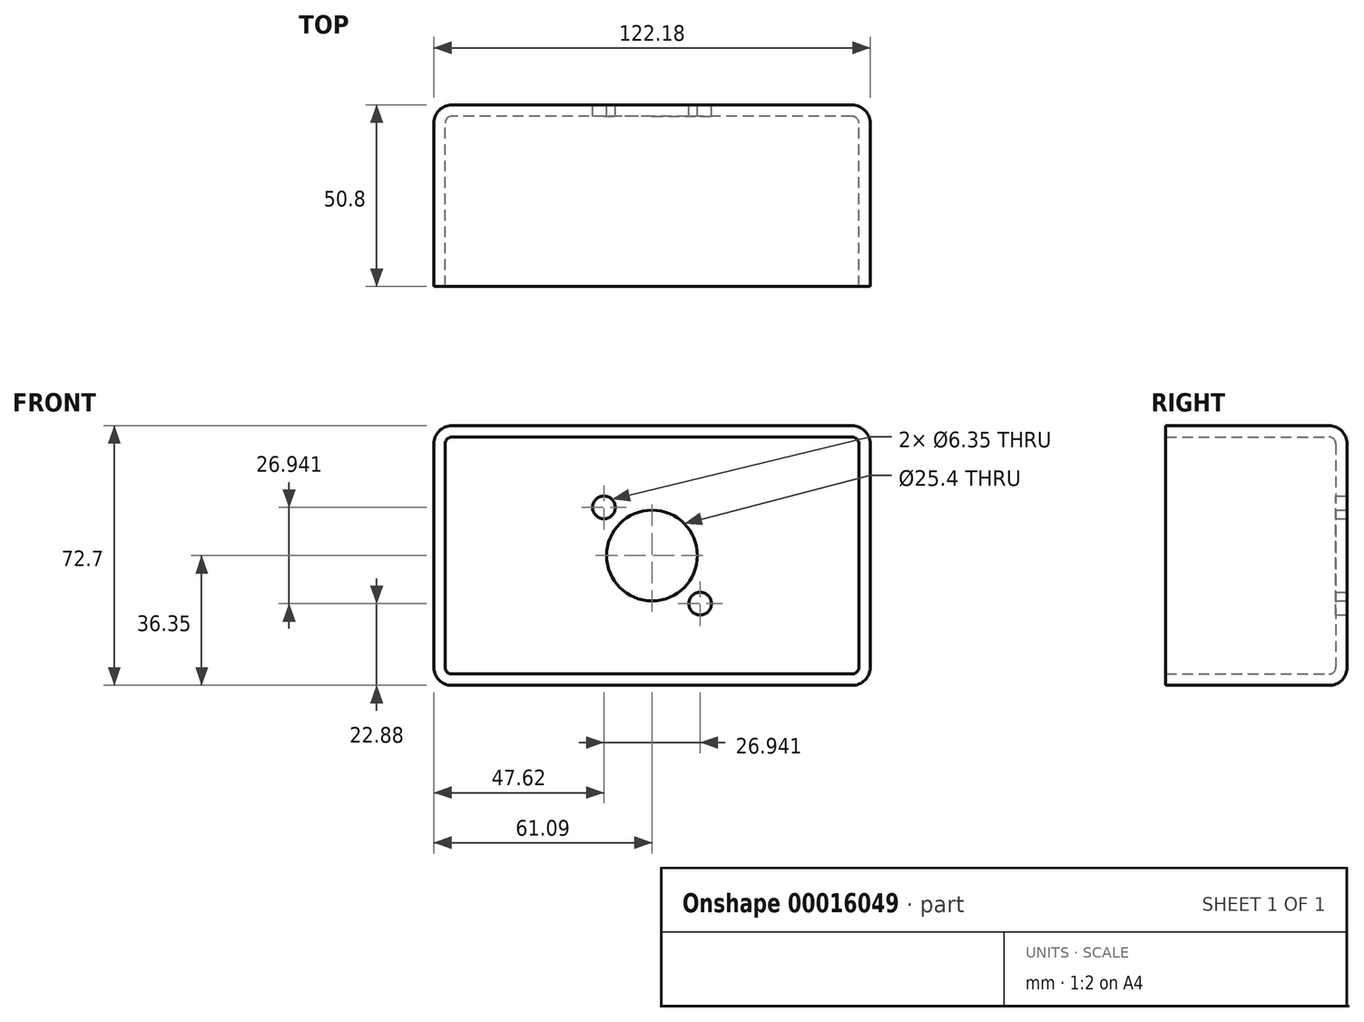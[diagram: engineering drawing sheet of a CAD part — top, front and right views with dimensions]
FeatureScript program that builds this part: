
annotation { "Feature Type Name" : "Feature", "Feature Type Description" : "" }
export const myFeature = defineFeature(function(context is Context, id is Id, definition is map)
    precondition{}
    {
        {
            var Q0;
            Q0=qCreatedBy(makeId("Front.planeOp"),FACE);
            var sketch = newSketch(context, id + "F0", { "sketchPlane" : qUnion([Q0])});
            skLineSegment(sketch, "E0.rect.bottom", {"start": v(61.09, 36.35) * mm, "end": v(-61.09, 36.35) * mm});
            skLineSegment(sketch, "E0.rect.top", {"start": v(61.09, -36.35) * mm, "end": v(-61.09, -36.35) * mm});
            skLineSegment(sketch, "E0.rect.left", {"start": v(61.09, 36.35) * mm, "end": v(61.09, -36.35) * mm});
            skLineSegment(sketch, "E0.rect.right", {"start": v(-61.09, 36.35) * mm, "end": v(-61.09, -36.35) * mm});
            skPoint(sketch, "E0.rect.middle", {"position": v(0, 0) * mm});
            skSolve(sketch);
        }
        {
            var Q0;
            Q0=makeQuery(id+"F0.imprint","IMPRINT",FACE,{"disambiguationData":[TD([[makeQuery(id+"F0.imprint","IMPRINT",EDGE,{"derivedFrom":sQuery(id+"F0.wireOp",EDGE,"E0.rect.bottom")}),1.0]])]});
            extrude(context, id + "F1", {"entities" : qUnion([Q0]), "depth" : 50.8 * mm});
        }
        {
            var Q0;
            Q0=makeQuery(id+"F1.opExtrude","CAP_FACE",FACE,{"disambiguationData":[OSD([sQuery(id+"F0.wireOp",EDGE,"E0.rect.bottom"),sQuery(id+"F0.wireOp",EDGE,"E0.rect.top"),sQuery(id+"F0.wireOp",EDGE,"E0.rect.left"),sQuery(id+"F0.wireOp",EDGE,"E0.rect.right")])],"isStart":false});
            shell(context, id + "F2", {"entities" : qUnion([Q0]), "thickness" : 3.17 * mm});
        }
        {
            var Q0;
            Q0=makeQuery(id+"F2.opShell","OFFSET_EDGE",EDGE,{"disambiguationData":[OSD([sQuery(id+"F0.wireOp",EDGE,"E0.rect.top"),sQuery(id+"F0.wireOp",EDGE,"E0.rect.left")])]});
            var Q1;
            Q1=makeQuery(id+"F2.opShell","OFFSET_FACE",FACE,{"disambiguationData":[OSD([sQuery(id+"F0.wireOp",EDGE,"E0.rect.bottom"),sQuery(id+"F0.wireOp",EDGE,"E0.rect.top"),sQuery(id+"F0.wireOp",EDGE,"E0.rect.left"),sQuery(id+"F0.wireOp",EDGE,"E0.rect.right")])]});
            var Q2;
            Q2=makeQuery(id+"F2.opShell","OFFSET_EDGE",EDGE,{"disambiguationData":[OSD([sQuery(id+"F0.wireOp",EDGE,"E0.rect.top"),sQuery(id+"F0.wireOp",EDGE,"E0.rect.right")])]});
            var Q3;
            Q3=makeQuery(id+"F2.opShell","OFFSET_EDGE",EDGE,{"disambiguationData":[OSD([sQuery(id+"F0.wireOp",EDGE,"E0.rect.bottom"),sQuery(id+"F0.wireOp",EDGE,"E0.rect.right")])]});
            var Q4;
            Q4=makeQuery(id+"F2.opShell","OFFSET_EDGE",EDGE,{"disambiguationData":[OSD([sQuery(id+"F0.wireOp",EDGE,"E0.rect.bottom"),sQuery(id+"F0.wireOp",EDGE,"E0.rect.left")])]});
            fillet(context, id + "F3", {"entities" : qUnion([Q0, Q1, Q2, Q3, Q4]), "radius" : 1.9 * mm, "tangentPropagation" : true, "allowEdgeOverflow" : false});
        }
        {
            var Q0;
            Q0=makeQuery(id+"F1.opExtrude","SWEPT_EDGE",EDGE,{"disambiguationData":[OSD([sQuery(id+"F0.wireOp",EDGE,"E0.rect.bottom"),sQuery(id+"F0.wireOp",EDGE,"E0.rect.left")])]});
            var Q1;
            Q1=makeQuery(id+"F1.opExtrude","SWEPT_EDGE",EDGE,{"disambiguationData":[OSD([sQuery(id+"F0.wireOp",EDGE,"E0.rect.top"),sQuery(id+"F0.wireOp",EDGE,"E0.rect.left")])]});
            var Q2;
            Q2=makeQuery(id+"F1.opExtrude","SWEPT_EDGE",EDGE,{"disambiguationData":[OSD([sQuery(id+"F0.wireOp",EDGE,"E0.rect.bottom"),sQuery(id+"F0.wireOp",EDGE,"E0.rect.right")])]});
            var Q3;
            Q3=makeQuery(id+"F1.opExtrude","SWEPT_EDGE",EDGE,{"disambiguationData":[OSD([sQuery(id+"F0.wireOp",EDGE,"E0.rect.top"),sQuery(id+"F0.wireOp",EDGE,"E0.rect.right")])]});
            var Q4;
            Q4=makeQuery(id+"F1.opExtrude","CAP_EDGE",EDGE,{"disambiguationData":[OSD([sQuery(id+"F0.wireOp",EDGE,"E0.rect.bottom")])],"isStart":true});
            var Q5;
            Q5=makeQuery(id+"F1.opExtrude","CAP_EDGE",EDGE,{"disambiguationData":[OSD([sQuery(id+"F0.wireOp",EDGE,"E0.rect.right")])],"isStart":true});
            var Q6;
            Q6=makeQuery(id+"F1.opExtrude","CAP_EDGE",EDGE,{"disambiguationData":[OSD([sQuery(id+"F0.wireOp",EDGE,"E0.rect.top")])],"isStart":true});
            var Q7;
            Q7=makeQuery(id+"F1.opExtrude","CAP_EDGE",EDGE,{"disambiguationData":[OSD([sQuery(id+"F0.wireOp",EDGE,"E0.rect.left")])],"isStart":true});
            var Q8;
            Q8=makeQuery(id+"F1.opExtrude","CAP_FACE",FACE,{"disambiguationData":[OSD([sQuery(id+"F0.wireOp",EDGE,"E0.rect.bottom"),sQuery(id+"F0.wireOp",EDGE,"E0.rect.top"),sQuery(id+"F0.wireOp",EDGE,"E0.rect.left"),sQuery(id+"F0.wireOp",EDGE,"E0.rect.right")])],"isStart":true});
            fillet(context, id + "F4", {"entities" : qUnion([Q0, Q1, Q2, Q3, Q4, Q5, Q6, Q7, Q8]), "radius" : 5.08 * mm, "tangentPropagation" : true, "allowEdgeOverflow" : false});
        }
        {
            var Q0;
            Q0=makeQuery(id+"F1.opExtrude","CAP_FACE",FACE,{"disambiguationData":[OSD([sQuery(id+"F0.wireOp",EDGE,"E0.rect.bottom"),sQuery(id+"F0.wireOp",EDGE,"E0.rect.top"),sQuery(id+"F0.wireOp",EDGE,"E0.rect.left"),sQuery(id+"F0.wireOp",EDGE,"E0.rect.right")])],"isStart":true});
            var sketch = newSketch(context, id + "F5", { "sketchPlane" : qUnion([Q0])});
            skLineSegment(sketch, "E1", {"start": v(-56, 0) * mm, "end": v(56, 0) * mm, "construction": true});
            skCircle(sketch, "E2", {"center": v(0, 0) * mm, "radius": 12.7 * mm});
            skLineSegment(sketch, "E3", {"start": v(-13.47, -13.47) * mm, "end": v(13.47, 13.47) * mm, "construction": true});
            skCircle(sketch, "E4", {"center": v(13.47, 13.47) * mm, "radius": 3.18 * mm});
            skCircle(sketch, "E5", {"center": v(-13.47, -13.47) * mm, "radius": 3.18 * mm});
            skSolve(sketch);
        }
        {
            var Q0;
            Q0=makeQuery(id+"F5.imprint","IMPRINT",FACE,{"disambiguationData":[TD([[makeQuery(id+"F5.imprint","IMPRINT",EDGE,{"derivedFrom":sQuery(id+"F5.wireOp",EDGE,"E2")}),1.0]])]});
            var Q1;
            Q1=makeQuery(id+"F5.imprint","IMPRINT",FACE,{"disambiguationData":[TD([[makeQuery(id+"F5.imprint","IMPRINT",EDGE,{"derivedFrom":sQuery(id+"F5.wireOp",EDGE,"E4")}),1.0]])]});
            var Q2;
            Q2=makeQuery(id+"F5.imprint","IMPRINT",FACE,{"disambiguationData":[TD([[makeQuery(id+"F5.imprint","IMPRINT",EDGE,{"derivedFrom":sQuery(id+"F5.wireOp",EDGE,"E5")}),1.0]])]});
            extrude(context, id + "F6", {"entities" : qUnion([Q0, Q1, Q2]), "operationType" : NewBodyOperationType.REMOVE, "endBound" : BoundingType.UP_TO_NEXT, "oppositeDirection" : true, "depth" : 25.4 * mm});
        }
    });
